# Revit family: Коммутаторная коробка
name_source: partatom
category: Устройства вызова и оповещения
revit_build: Autodesk Revit 2017 (Build: 20170118_1100(x64)
units: mm (PartAtom-declared; Revit-internal decimal feet)

## family parameters
Всегда вертикально = Да
На основе рабочей плоскости = Нет
Общий = Нет
При загрузке вырезать с полостями = Нет
Размер круглого соединителя = Использовать диаметр
Сохранять ориентацию аннотаций = Нет
Тип детали = Нормальный
Точка расчета площади = Нет

## types (8) — shared parameters
ADSK_Завод-изготовитель = ELTIS
URL = https://www.eltis.com
Длина = 136 мм
Толщина = 29 мм
Ширина = 80 мм
zero-valued in all types: Ноль

## per-type parameters (varying)
| type | ADSK_Марка | ADSK_Масса | ADSK_Наименование краткое | ADSK_Обозначение | Комментарии к типоразмеру |
| Видеокоммутатор VC4/1-3 | VC4/1-3 | 0.13 | Видеокоммутатор | VC4/1-3 |  |
| Видеоразветвитель VS1/4-4 | VS1/4-4 | 0.09 | Видеоразветвитель | VS1/4-4 |  |
| Коммутатор этажный KMF-4.1 | KMF-4.1 | 0.13 | Коммутатор этажный | KMF-4.1 |  |
| Усилитель UD-SA-1 | UD-SA-1 | 0.12 | Усилитель | UD-SA-1 |  |
| Блок сопряжения ADC248-2 | ADC248-2 | 0.13 | Блок сопряжения | ADC248-2 | https://www.eltis.com |
| Коммутатор блока вызова КМ500-8.3Т | КМ500-8.3Т | 0.16 | Коммутатор блока вызова | КМ500-8.3Т |  |
| Видеоразветвитель VS1/4-2 | VS1/4-2 | 0.13 | Видеоразветвитель | VS1/4-2 |  |
| Коммутатор этажный KMF-6.1 | KMF-6.1 | 0.13 | Коммутатор этажный | KMF-6.1 |  |

note: column(s) folded — value = type name in every type: ADSK_Наименование, Описание

## geometry (parser evidence)
native form markers: Blend x2
no freeform markers — native parametric forms only
